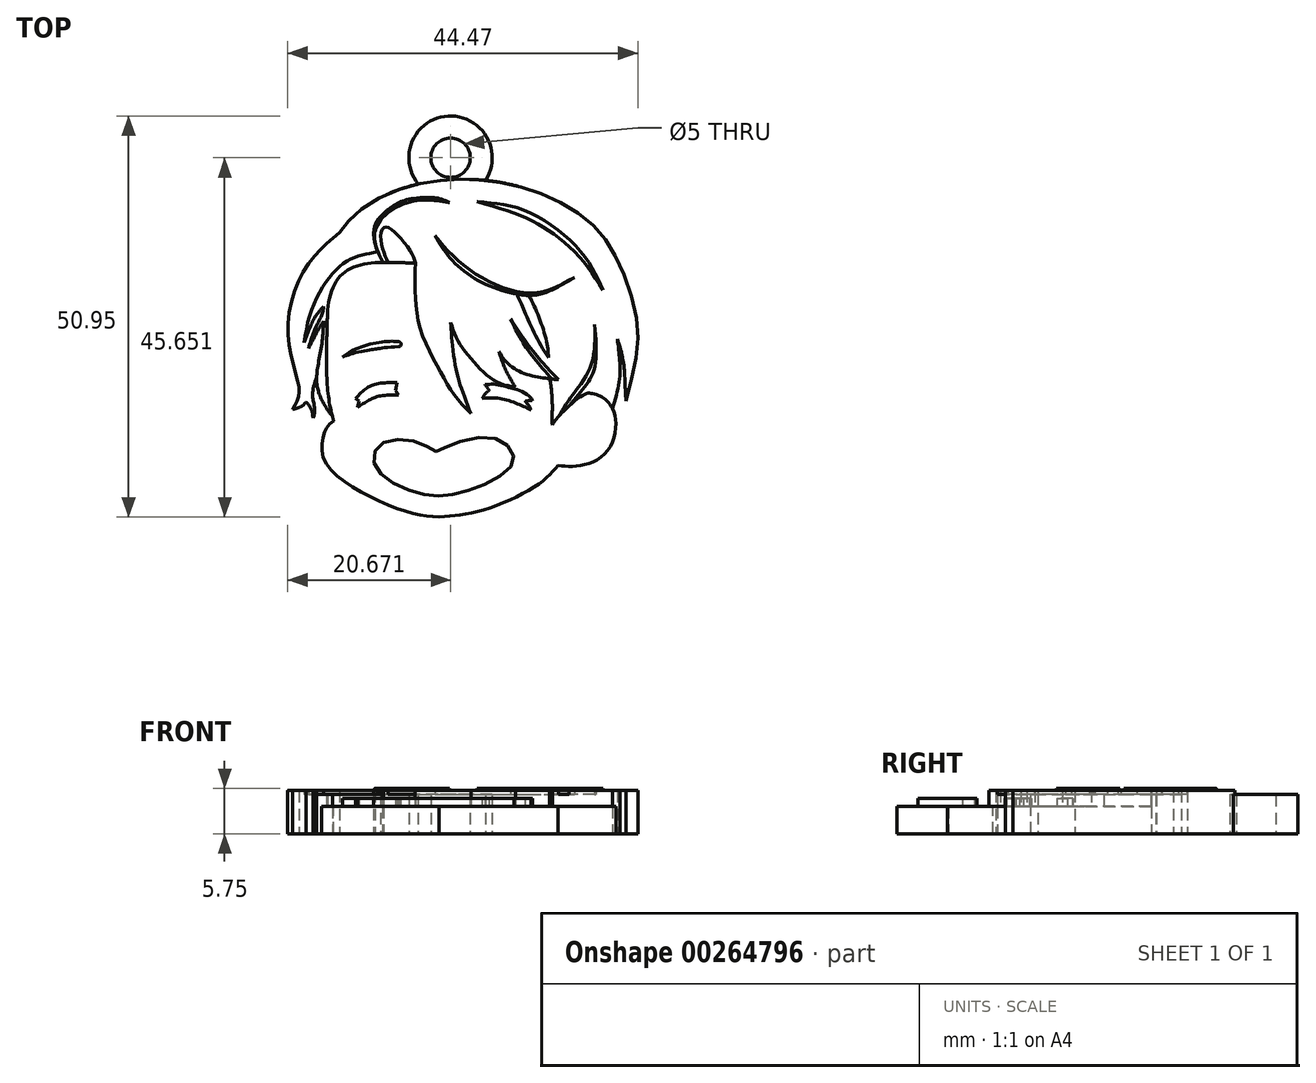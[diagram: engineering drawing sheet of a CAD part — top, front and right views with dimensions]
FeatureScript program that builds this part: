
annotation { "Feature Type Name" : "Feature", "Feature Type Description" : "" }
export const myFeature = defineFeature(function(context is Context, id is Id, definition is map)
    precondition{}
    {
        {
            var Q0;
            Q0=qCreatedBy(makeId("Top.planeOp"),FACE);
            var sketch = newSketch(context, id + "F0", { "sketchPlane" : qUnion([Q0])});
            skLineSegment(sketch, "E0", {"start": v(0, 26.14) * mm, "end": v(0, -13.86) * mm, "construction": true});
            skFitSpline(sketch, "E1", {"points": [v(-13.4, -3.41) * mm, v(-14.59, -4.9) * mm, v(-14.68, -8.16) * mm, v(-10.4, -12.17) * mm, v(-3.68, -15.06) * mm, v(0, -15.62) * mm], "startDerivative": vector(-13.93, -9.32) * mm, "endDerivative": vector(18.39, -1.5) * mm});
            skFitSpline(sketch, "E2", {"points": [v(0, -15.62) * mm, v(5.36, -14.78) * mm, v(12.63, -11.43) * mm, v(15.05, -9.1) * mm], "startDerivative": vector(14.98, 1.14) * mm, "endDerivative": vector(7.26, 8.68) * mm});
            skFitSpline(sketch, "E3", {"points": [v(15.05, -9.1) * mm, v(17.76, -9.1) * mm, v(21.2, -7.42) * mm, v(22.42, -3.41) * mm, v(21.58, -1.17) * mm, v(18.5, 0) * mm, v(15.05, -3.41) * mm, v(15.05, -4.25) * mm], "startDerivative": vector(18.97, -1.5) * mm, "endDerivative": vector(3.2, -10.24) * mm, "construction": true});
            skFitSpline(sketch, "E4", {"points": [v(14.37, -3.91) * mm, v(15.86, -2.1) * mm, v(18.5, 0) * mm, v(19.35, 0.08) * mm, v(20.48, -0.29) * mm, v(21.58, -1.17) * mm, v(22.42, -3.41) * mm, v(21.2, -7.42) * mm, v(17.76, -9.1) * mm, v(15.05, -9.1) * mm], "startDerivative": vector(9.94, 16.2) * mm, "endDerivative": vector(-21.45, 1.73) * mm});
            skFitSpline(sketch, "E5", {"points": [v(-14.19, 10.66) * mm, v(-12.54, 15.05) * mm, v(-8.76, 16.63) * mm, v(-3.04, 16.63) * mm], "startDerivative": vector(1.75, 16.5) * mm, "endDerivative": vector(16.06, -0.48) * mm});
            skFitSpline(sketch, "E6", {"points": [v(-3.04, 16.63) * mm, v(-3.04, 12.63) * mm, v(-2.33, 8) * mm, v(0, 3.15) * mm, v(1.82, 0) * mm, v(4.02, -2.5) * mm], "startDerivative": vector(-0.37, -20.1) * mm, "endDerivative": vector(13.1, -13.51) * mm});
            skFitSpline(sketch, "E7", {"points": [v(4.02, -2.5) * mm, v(2.77, 0.87) * mm, v(1.98, 3.93) * mm, v(1.56, 7.52) * mm, v(1.43, 9.09) * mm], "startDerivative": vector(-5.05, 13.03) * mm, "endDerivative": vector(-1.35, 13.2) * mm});
            skFitSpline(sketch, "E8", {"points": [v(1.43, 9.09) * mm, v(2.5, 6.55) * mm, v(4.66, 3.77) * mm, v(7.17, 1.61) * mm, v(9.69, 0.87) * mm], "startDerivative": vector(3.7, -10.7) * mm, "endDerivative": vector(11.1, -2.02) * mm});
            skFitSpline(sketch, "E9", {"points": [v(7.82, 5.39) * mm, v(9.13, 3.52) * mm, v(11.7, 2.36) * mm, v(15.14, 1.84) * mm, v(17.15, 1.84) * mm], "startDerivative": vector(4.7, -8.74) * mm, "endDerivative": vector(8.44, 0.3) * mm, "construction": true});
            skFitSpline(sketch, "E10", {"points": [v(14.01, 1.94) * mm, v(14.2, 0.87) * mm, v(14.32, -0.49) * mm, v(14.36, -2.2) * mm, v(14.37, -3.91) * mm], "startDerivative": vector(1.08, -4.56) * mm, "endDerivative": vector(1.1, -5.47) * mm});
            skFitSpline(sketch, "E11", {"points": [v(-13.4, -3.41) * mm, v(-14.31, 2.85) * mm, v(-14.19, 10.66) * mm], "startDerivative": vector(-3.96, 12.36) * mm, "endDerivative": vector(0.4, 15.4) * mm});
            skFitSpline(sketch, "E12", {"points": [v(-12.65, 20.52) * mm, v(-16.75, 16.37) * mm, v(-19.24, 8.2) * mm, v(-17.95, 1.51) * mm, v(-17.9, -0.43) * mm, v(-18.62, -1.94) * mm], "startDerivative": vector(-19.1, -15.5) * mm, "endDerivative": vector(-7.31, -11.74) * mm});
            skFitSpline(sketch, "E13", {"points": [v(-18.62, -1.94) * mm, v(-17.47, -1.53) * mm, v(-16.9, -0.98) * mm], "startDerivative": vector(2.3, 0.41) * mm, "endDerivative": vector(1.1, 1.36) * mm});
            skFitSpline(sketch, "E14", {"points": [v(-16.9, -0.98) * mm, v(-16.25, -1.94) * mm, v(-16.04, -3.02) * mm], "startDerivative": vector(1.51, -1.67) * mm, "endDerivative": vector(0.4, -2.4) * mm});
            skFitSpline(sketch, "E15", {"points": [v(-16.04, -3.02) * mm, v(-15.81, -1.94) * mm, v(-16.04, -0.8) * mm], "startDerivative": vector(0.92, 2.4) * mm, "endDerivative": vector(-0.88, 2.92) * mm, "construction": true});
            skFitSpline(sketch, "E16", {"points": [v(-16.04, -0.8) * mm, v(-16.04, 0.6) * mm, v(-15.58, 1.39) * mm], "startDerivative": vector(-0.2, 1.92) * mm, "endDerivative": vector(0.95, 1.57) * mm, "construction": true});
            skFitSpline(sketch, "E17", {"points": [v(-12.65, 20.52) * mm, v(-10.64, 22.9) * mm, v(-5.79, 25.74) * mm, v(0, 27.11) * mm, v(5.19, 27.21) * mm, v(10.8, 26.19) * mm, v(16.16, 23.92) * mm, v(20.2, 20.77) * mm, v(22.7, 16.89) * mm, v(24.9, 10.6) * mm, v(25.08, 5.27) * mm, v(23.71, -0.85) * mm], "startDerivative": vector(24.35, 34.26) * mm, "endDerivative": vector(-17.15, -63.7) * mm});
            skFitSpline(sketch, "E18", {"points": [v(22.61, 7) * mm, v(23.36, 4.37) * mm, v(23.57, 1.98) * mm, v(23.71, -0.85) * mm], "startDerivative": vector(2.65, -7.12) * mm, "endDerivative": vector(0.34, -7.37) * mm});
            skFitSpline(sketch, "E19", {"points": [v(22.61, 7) * mm, v(22.88, 4.69) * mm, v(22.88, 1.75) * mm, v(22.29, -1.24) * mm, v(22.05, -1.84) * mm], "startDerivative": vector(1.12, -8.58) * mm, "endDerivative": vector(-1.44, -3.33) * mm, "construction": true});
            skFitSpline(sketch, "E20", {"points": [v(22, -1.84) * mm, v(22.88, 1.75) * mm, v(22.88, 4.69) * mm, v(22.61, 7) * mm], "startDerivative": vector(2.87, 9.77) * mm, "endDerivative": vector(-1, 7.59) * mm});
            skFitSpline(sketch, "E21", {"points": [v(-15.58, 1.39) * mm, v(-15.19, -0.15) * mm, v(-14.34, -1.78) * mm, v(-13.58, -2.82) * mm], "startDerivative": vector(0.86, -4.54) * mm, "endDerivative": vector(2.6, -3.14) * mm});
            skFitSpline(sketch, "E22", {"points": [v(-10.64, -0.53) * mm, v(-9.31, 0.69) * mm, v(-7.93, 1.32) * mm, v(-5.39, 1.45) * mm], "startDerivative": vector(4.08, 4.14) * mm, "endDerivative": vector(7.18, -0.06) * mm});
            skFitSpline(sketch, "E23", {"points": [v(-10.64, -0.53) * mm, v(-10.2, -0.88) * mm], "startDerivative": vector(0.44, -0.35) * mm, "endDerivative": vector(0.44, -0.35) * mm});
            skFitSpline(sketch, "E24", {"points": [v(-10.2, -0.88) * mm, v(-10.4, -1.72) * mm], "startDerivative": vector(-0.2, -0.84) * mm, "endDerivative": vector(-0.2, -0.84) * mm});
            skFitSpline(sketch, "E25", {"points": [v(-10.4, -1.72) * mm, v(-9.13, -0.88) * mm, v(-7.65, -0.27) * mm, v(-5.2, -0.09) * mm], "startDerivative": vector(4.13, 2.9) * mm, "endDerivative": vector(6.8, 0.1) * mm});
            skFitSpline(sketch, "E26", {"points": [v(-5.39, 1.45) * mm, v(-5.55, 0.46) * mm], "startDerivative": vector(-0.16, -0.99) * mm, "endDerivative": vector(-0.16, -0.99) * mm});
            skFitSpline(sketch, "E27", {"points": [v(-5.55, 0.46) * mm, v(-5.2, -0.09) * mm], "startDerivative": vector(0.36, -0.54) * mm, "endDerivative": vector(0.36, -0.54) * mm});
            skFitSpline(sketch, "E28", {"points": [v(5.8, 1.2) * mm, v(7.17, 1.23) * mm, v(8.9, 0.84) * mm, v(10.2, 0.46) * mm, v(11.7, -0.53) * mm, v(11.82, -0.85) * mm], "startDerivative": vector(6.24, 0.69) * mm, "endDerivative": vector(0.25, -2.75) * mm});
            skFitSpline(sketch, "E29", {"points": [v(11.82, -0.85) * mm, v(11.29, -0.85) * mm, v(10.9, -0.92) * mm], "startDerivative": vector(-1.03, 0.04) * mm, "endDerivative": vector(-0.8, -0.2) * mm});
            skFitSpline(sketch, "E30", {"points": [v(10.9, -0.92) * mm, v(11.16, -1.19) * mm, v(11.5, -1.66) * mm, v(11.63, -2) * mm], "startDerivative": vector(0.8, -0.75) * mm, "endDerivative": vector(0.3, -1.03) * mm});
            skFitSpline(sketch, "E31", {"points": [v(11.63, -2) * mm, v(9.93, -1.23) * mm, v(7.6, -0.53) * mm, v(5.46, -0.53) * mm], "startDerivative": vector(-5.2, 2.45) * mm, "endDerivative": vector(-6.32, -0.48) * mm});
            skFitSpline(sketch, "E32", {"points": [v(5.8, 1.2) * mm, v(6.08, 0.86) * mm, v(6.35, 0.46) * mm], "startDerivative": vector(0.58, -0.66) * mm, "endDerivative": vector(0.51, -0.8) * mm});
            skFitSpline(sketch, "E33", {"points": [v(6.35, 0.46) * mm, v(5.9, 0.11) * mm, v(5.46, -0.53) * mm], "startDerivative": vector(-1.02, -0.57) * mm, "endDerivative": vector(-0.76, -1.38) * mm});
            skFitSpline(sketch, "E34", {"points": [v(-5.16, 6.68) * mm, v(-7.38, 6.62) * mm, v(-10.76, 5.64) * mm, v(-12.27, 4.73) * mm], "startDerivative": vector(-6.43, 0.3) * mm, "endDerivative": vector(-4.54, -3.28) * mm});
            skFitSpline(sketch, "E35", {"points": [v(-12.27, 4.73) * mm, v(-10.8, 5.2) * mm, v(-8.63, 5.65) * mm, v(-7.81, 5.78) * mm, v(-5.17, 6.02) * mm], "startDerivative": vector(5, 2.04) * mm, "endDerivative": vector(12.14, 0.39) * mm});
            skFitSpline(sketch, "E36", {"points": [v(-5.16, 6.68) * mm, v(-4.88, 6.48) * mm, v(-4.89, 6.15) * mm, v(-5.17, 6.02) * mm], "startDerivative": vector(1, -0.45) * mm, "endDerivative": vector(-1.03, -0.24) * mm});
            skFitSpline(sketch, "E37", {"points": [v(11.13, 4.5) * mm, v(8.62, 5.65) * mm, v(5.33, 6.3) * mm, v(3.94, 6.2) * mm, v(3.94, 5.88) * mm, v(6.12, 5.78) * mm, v(8.1, 5.39) * mm, v(11.13, 4.5) * mm]});
            skFitSpline(sketch, "E38", {"points": [v(-0.4, -7.32) * mm, v(-1.95, -6.4) * mm, v(-5.02, -5.77) * mm, v(-7.66, -6.54) * mm, v(-8.33, -8.3) * mm, v(-7.24, -10.32) * mm, v(-4.17, -12.08) * mm, v(-0.79, -12.9) * mm, v(1.96, -12.72) * mm, v(5.77, -11.45) * mm, v(8.91, -9.44) * mm, v(9.44, -7.78) * mm, v(8.1, -6.09) * mm, v(4.82, -5.52) * mm, v(0.45, -6.9) * mm, v(-0.4, -7.32) * mm]});
            skLineSegment(sketch, "E39.bottom", {"start": v(-9.61, -2.71) * mm, "end": v(-9.4, -2.71) * mm});
            skLineSegment(sketch, "E39.top", {"start": v(-9.61, -3.67) * mm, "end": v(-9.4, -3.67) * mm});
            skLineSegment(sketch, "E39.left", {"start": v(-9.61, -2.71) * mm, "end": v(-9.61, -3.67) * mm});
            skLineSegment(sketch, "E39.right", {"start": v(-9.4, -2.71) * mm, "end": v(-9.4, -3.67) * mm});
            skLineSegment(sketch, "E40.bottom", {"start": v(-8.16, -2.58) * mm, "end": v(-7.95, -2.58) * mm});
            skLineSegment(sketch, "E40.top", {"start": v(-8.16, -3.65) * mm, "end": v(-7.95, -3.65) * mm});
            skLineSegment(sketch, "E40.left", {"start": v(-8.16, -2.58) * mm, "end": v(-8.16, -3.65) * mm});
            skLineSegment(sketch, "E40.right", {"start": v(-7.95, -2.58) * mm, "end": v(-7.95, -3.65) * mm});
            skLineSegment(sketch, "E41.bottom", {"start": v(-6.18, -2.56) * mm, "end": v(-5.92, -2.56) * mm});
            skLineSegment(sketch, "E41.top", {"start": v(-6.18, -3.57) * mm, "end": v(-5.92, -3.57) * mm});
            skLineSegment(sketch, "E41.left", {"start": v(-6.18, -2.56) * mm, "end": v(-6.18, -3.57) * mm});
            skLineSegment(sketch, "E41.right", {"start": v(-5.92, -2.56) * mm, "end": v(-5.92, -3.57) * mm});
            skLineSegment(sketch, "E42.bottom", {"start": v(7.82, -3.54) * mm, "end": v(8.22, -3.54) * mm});
            skLineSegment(sketch, "E42.top", {"start": v(7.82, -4.76) * mm, "end": v(8.22, -4.76) * mm});
            skLineSegment(sketch, "E42.left", {"start": v(7.82, -3.54) * mm, "end": v(7.82, -4.76) * mm});
            skLineSegment(sketch, "E42.right", {"start": v(8.22, -3.54) * mm, "end": v(8.22, -4.76) * mm});
            skLineSegment(sketch, "E43.bottom", {"start": v(9.06, -3.54) * mm, "end": v(9.53, -3.54) * mm});
            skLineSegment(sketch, "E43.top", {"start": v(9.06, -4.83) * mm, "end": v(9.53, -4.83) * mm});
            skLineSegment(sketch, "E43.left", {"start": v(9.06, -3.54) * mm, "end": v(9.06, -4.83) * mm});
            skLineSegment(sketch, "E43.right", {"start": v(9.53, -3.54) * mm, "end": v(9.53, -4.83) * mm});
            skLineSegment(sketch, "E44.bottom", {"start": v(10.28, -3.46) * mm, "end": v(10.68, -3.46) * mm});
            skLineSegment(sketch, "E44.top", {"start": v(10.28, -4.8) * mm, "end": v(10.68, -4.8) * mm});
            skLineSegment(sketch, "E44.left", {"start": v(10.28, -3.46) * mm, "end": v(10.28, -4.8) * mm});
            skLineSegment(sketch, "E44.right", {"start": v(10.68, -3.46) * mm, "end": v(10.68, -4.8) * mm});
            skFitSpline(sketch, "E45", {"points": [v(-7.1, 16.74) * mm, v(-8, 18.64) * mm, v(-8.06, 21.96) * mm, v(-5.99, 24.33) * mm, v(-0.95, 24.57) * mm, v(1.6, 21.24) * mm, v(5.16, 17.15) * mm, v(11.1, 14.6) * mm, v(17.2, 14.84) * mm], "startDerivative": vector(-11.68, 19.6) * mm, "endDerivative": vector(41.04, 5.62) * mm});
            skFitSpline(sketch, "E46", {"points": [v(-2.9, 17.32) * mm, v(-3.04, 16.63) * mm], "startDerivative": vector(-0.15, -0.7) * mm, "endDerivative": vector(-0.15, -0.7) * mm});
            skFitSpline(sketch, "E47", {"points": [v(0.94, 15.14) * mm, v(1.16, 10.73) * mm, v(1.43, 9.09) * mm], "startDerivative": vector(0.23, -8) * mm, "endDerivative": vector(0.78, -3.78) * mm});
            skFitSpline(sketch, "E48", {"points": [v(9.69, 0.87) * mm, v(8.23, 3.55) * mm, v(6.79, 8.4) * mm, v(6.2, 11.37) * mm, v(5.56, 13.76) * mm], "startDerivative": vector(-6.27, 9.9) * mm, "endDerivative": vector(-3.25, 11.04) * mm});
            skFitSpline(sketch, "E49", {"points": [v(7.57, 5.4) * mm, v(9.13, 3.52) * mm, v(11.7, 2.36) * mm, v(14.01, 1.94) * mm, v(15.14, 1.84) * mm, v(17.15, 1.84) * mm], "startDerivative": vector(6.28, -9.53) * mm, "endDerivative": vector(11.25, 0.15) * mm});
            skFitSpline(sketch, "E50", {"points": [v(-8.36, 17.98) * mm, v(-12.22, 16.56) * mm, v(-16.6, 9.44) * mm, v(-17.2, 0.6) * mm, v(-16.9, -0.98) * mm], "startDerivative": vector(-17.57, -3.44) * mm, "endDerivative": vector(2.33, -8.82) * mm});
            skFitSpline(sketch, "E51", {"points": [v(-7.82, 18.1) * mm, v(-8.36, 17.98) * mm], "startDerivative": vector(-0.55, -0.12) * mm, "endDerivative": vector(-0.55, -0.12) * mm});
            skFitSpline(sketch, "E52", {"points": [v(-12.65, 20.52) * mm, v(-11.54, 21.12) * mm, v(-10.45, 21.41) * mm, v(-9.17, 21.45) * mm, v(-8.2, 21.3) * mm], "startDerivative": vector(5.65, 3.37) * mm, "endDerivative": vector(3.5, -0.93) * mm});
            skFitSpline(sketch, "E53", {"points": [v(18.77, 12.31) * mm, v(20.73, 10.42) * mm, v(22.61, 7) * mm], "startDerivative": vector(4.5, -3.68) * mm, "endDerivative": vector(3.22, -6.86) * mm});
            skFitSpline(sketch, "E54", {"points": [v(4.81, 24.45) * mm, v(11.09, 23.23) * mm, v(17.96, 18.13) * mm, v(20.81, 13.21) * mm], "startDerivative": vector(19.97, -1.65) * mm, "endDerivative": vector(7.33, -16.32) * mm});
            skFitSpline(sketch, "E55", {"points": [v(4.81, 24.45) * mm, v(10.55, 22.58) * mm, v(14.29, 20.5) * mm, v(17.96, 17.25) * mm, v(20.81, 13.21) * mm], "startDerivative": vector(23.36, -6.63) * mm, "endDerivative": vector(10.67, -16.96) * mm});
            skFitSpline(sketch, "E56", {"points": [v(-6.5, 16.74) * mm, v(-7.18, 18.45) * mm, v(-7.36, 20.62) * mm, v(-6.8, 21.21) * mm, v(-5.61, 20.53) * mm, v(-3.63, 18.1) * mm, v(-3.04, 16.63) * mm], "startDerivative": vector(-4.34, 9.22) * mm, "endDerivative": vector(2.53, -8.61) * mm});
            skFitSpline(sketch, "E57", {"points": [v(-2.59, 20.74) * mm, v(-2.9, 17.32) * mm], "startDerivative": vector(-0.3, -3.41) * mm, "endDerivative": vector(-0.3, -3.41) * mm});
            skFitSpline(sketch, "E58", {"points": [v(-0.51, 20.11) * mm, v(2.78, 16.63) * mm, v(7.79, 13.65) * mm, v(12.74, 12.94) * mm, v(17.2, 14.84) * mm], "startDerivative": vector(12.39, -14.82) * mm, "endDerivative": vector(17.86, 10.14) * mm});
            skFitSpline(sketch, "E59", {"points": [v(-0.51, 20.11) * mm, v(0.91, 17.86) * mm, v(4.65, 14.6) * mm, v(9.86, 12.7) * mm, v(13.16, 12.79) * mm, v(17.2, 14.84) * mm], "startDerivative": vector(7.39, -13.6) * mm, "endDerivative": vector(20.75, 11.78) * mm});
            skFitSpline(sketch, "E60", {"points": [v(0.94, 15.14) * mm, v(0.76, 17.22) * mm, v(0.38, 18.59) * mm], "startDerivative": vector(-0.2, 4.02) * mm, "endDerivative": vector(-0.94, 2.85) * mm});
            skFitSpline(sketch, "E61", {"points": [v(9.86, 12.7) * mm, v(10.79, 10.58) * mm, v(12.98, 6.07) * mm, v(15.58, 2.68) * mm, v(17.15, 1.84) * mm], "startDerivative": vector(3.94, -8.95) * mm, "endDerivative": vector(8.2, -3.2) * mm});
            skFitSpline(sketch, "E62", {"points": [v(13.87, 4.65) * mm, v(13.67, 6.45) * mm, v(12.7, 9.67) * mm, v(11.43, 12.54) * mm], "startDerivative": vector(-0.38, 6.12) * mm, "endDerivative": vector(-3.67, 7.7) * mm});
            skFitSpline(sketch, "E63", {"points": [v(9.07, 9.53) * mm, v(10.98, 6) * mm, v(14.32, 1.9) * mm], "startDerivative": vector(3.61, -7.54) * mm, "endDerivative": vector(6.8, -7.7) * mm});
            skFitSpline(sketch, "E64", {"points": [v(9.07, 9.53) * mm, v(12.15, 5.15) * mm, v(15.14, 1.84) * mm], "startDerivative": vector(5.78, -8.75) * mm, "endDerivative": vector(6.37, -6.58) * mm});
            skFitSpline(sketch, "E65", {"points": [v(19.74, 8.86) * mm, v(19.24, 3.54) * mm, v(16.86, -0.2) * mm, v(15.14, -2.86) * mm], "startDerivative": vector(0.33, -15.04) * mm, "endDerivative": vector(-5.4, -9.03) * mm});
            skFitSpline(sketch, "E66", {"points": [v(19.74, 8.86) * mm, v(19.74, 3.35) * mm, v(18.47, 0.94) * mm, v(16.49, -1.5) * mm], "startDerivative": vector(1.23, -15.1) * mm, "endDerivative": vector(-6.75, -8.1) * mm});
            skFitSpline(sketch, "E67", {"points": [v(-15.58, 1.39) * mm, v(-15.24, 3.23) * mm, v(-14.32, 5.78) * mm], "startDerivative": vector(0.5, 3.93) * mm, "endDerivative": vector(2, 4.83) * mm, "construction": true});
            skFitSpline(sketch, "E68", {"points": [v(-14.32, 6.05) * mm, v(-15.81, 1.46) * mm, v(-16.1, -0.15) * mm, v(-15.95, -1.08) * mm, v(-15.86, -2.42) * mm, v(-16.04, -3.02) * mm], "startDerivative": vector(-5.21, -14.88) * mm, "endDerivative": vector(-1.79, -4.23) * mm});
            skFitSpline(sketch, "E69", {"points": [v(-14.69, 11.1) * mm, v(-15.81, 9.72) * mm, v(-17.15, 6.53) * mm], "startDerivative": vector(-2.78, -2.86) * mm, "endDerivative": vector(-2.16, -6.12) * mm});
            skFitSpline(sketch, "E70", {"points": [v(-14.69, 11.1) * mm, v(-14.96, 9.97) * mm, v(-15.81, 8.24) * mm, v(-16.6, 5.78) * mm], "startDerivative": vector(-0.66, -4.16) * mm, "endDerivative": vector(-1.75, -6.5) * mm});
            skFitSpline(sketch, "E71", {"points": [v(-16.6, 5.78) * mm, v(-15.5, 7.96) * mm, v(-14.69, 9.26) * mm], "startDerivative": vector(2.02, 4.17) * mm, "endDerivative": vector(1.8, 2.73) * mm});
            skFitSpline(sketch, "E72", {"points": [v(-14.69, 9.26) * mm, v(-14.96, 6.05) * mm, v(-15.5, 3.02) * mm, v(-15.58, 1.39) * mm], "startDerivative": vector(-0.44, -8.55) * mm, "endDerivative": vector(0.02, -5.67) * mm});
            skFitSpline(sketch, "E73", {"points": [v(-7.1, 16.74) * mm, v(-7.82, 18.1) * mm, v(-8.2, 21.3) * mm, v(-5.99, 23.82) * mm, v(-4.13, 24.68) * mm, v(-0.57, 24.95) * mm, v(1.3, 24.33) * mm], "startDerivative": vector(-5.55, 8.97) * mm, "endDerivative": vector(12, -5.66) * mm});
            skFitSpline(sketch, "E74", {"points": [v(1.3, 24.33) * mm, v(-0.44, 24.6) * mm, v(-4.02, 24.33) * mm, v(-7.42, 22.13) * mm, v(-8.22, 19.85) * mm, v(-7.1, 16.57) * mm], "startDerivative": vector(-10.24, 2) * mm, "endDerivative": vector(7.31, -15.93) * mm});
            skSolve(sketch);
        }
        {
            var Q0;
            {var subQ4=sQuery(id+"F0.wireOp",EDGE,"E1");Q0=makeQuery(id+"F0.imprint","IMPRINT",FACE,{"disambiguationData":[TD([[makeQuery(id+"F0.imprint","IMPRINT",EDGE,{"derivedFrom":subQ4}),1.0]])]});}
            var Q1;
            Q1=makeQuery(id+"F0.imprint","IMPRINT",FACE,{"disambiguationData":[TD([[makeQuery(id+"F0.imprint","IMPRINT",EDGE,{"derivedFrom":sQuery(id+"F0.wireOp",EDGE,"E39.bottom")}),-1.0]])]});
            var Q2;
            Q2=makeQuery(id+"F0.imprint","IMPRINT",FACE,{"disambiguationData":[TD([[makeQuery(id+"F0.imprint","IMPRINT",EDGE,{"derivedFrom":sQuery(id+"F0.wireOp",EDGE,"E40.bottom")}),-1.0]])]});
            var Q3;
            Q3=makeQuery(id+"F0.imprint","IMPRINT",FACE,{"disambiguationData":[TD([[makeQuery(id+"F0.imprint","IMPRINT",EDGE,{"derivedFrom":sQuery(id+"F0.wireOp",EDGE,"E41.bottom")}),-1.0]])]});
            var Q4;
            Q4=makeQuery(id+"F0.imprint","IMPRINT",FACE,{"disambiguationData":[TD([[makeQuery(id+"F0.imprint","IMPRINT",EDGE,{"derivedFrom":sQuery(id+"F0.wireOp",EDGE,"E42.bottom")}),-1.0]])]});
            var Q5;
            Q5=makeQuery(id+"F0.imprint","IMPRINT",FACE,{"disambiguationData":[TD([[makeQuery(id+"F0.imprint","IMPRINT",EDGE,{"derivedFrom":sQuery(id+"F0.wireOp",EDGE,"E43.bottom")}),-1.0]])]});
            var Q6;
            Q6=makeQuery(id+"F0.imprint","IMPRINT",FACE,{"disambiguationData":[TD([[makeQuery(id+"F0.imprint","IMPRINT",EDGE,{"derivedFrom":sQuery(id+"F0.wireOp",EDGE,"E44.bottom")}),-1.0]])]});
            extrude(context, id + "F1", {"entities" : qUnion([Q0, Q1, Q2, Q3, Q4, Q5, Q6]), "depth" : 3.5 * mm, "offsetDistance" : 25 * mm});
        }
        {
            var Q0;
            Q0=makeQuery(id+"F0.imprint","IMPRINT",FACE,{"disambiguationData":[TD([[makeQuery(id+"F0.imprint","IMPRINT",EDGE,{"derivedFrom":sQuery(id+"F0.wireOp",EDGE,"E34")}),1.0]])]});
            var Q1;
            Q1=makeQuery(id+"F0.imprint","IMPRINT",FACE,{"disambiguationData":[TD([[makeQuery(id+"F0.imprint","IMPRINT",EDGE,{"derivedFrom":sQuery(id+"F0.wireOp",EDGE,"E38")}),1.0]])]});
            var Q2;
            Q2=makeQuery(id+"F0.imprint","IMPRINT",FACE,{"disambiguationData":[TD([[makeQuery(id+"F0.imprint","IMPRINT",EDGE,{"derivedFrom":sQuery(id+"F0.wireOp",EDGE,"E22")}),-1.0]])]});
            var Q3;
            Q3=makeQuery(id+"F0.imprint","IMPRINT",FACE,{"disambiguationData":[TD([[makeQuery(id+"F0.imprint","IMPRINT",EDGE,{"derivedFrom":sQuery(id+"F0.wireOp",EDGE,"E28")}),-1.0]])]});
            extrude(context, id + "F2", {"entities" : qUnion([Q0, Q1, Q2, Q3]), "operationType" : NewBodyOperationType.ADD, "depth" : 4.5 * mm, "offsetDistance" : 25 * mm});
        }
        {
            var Q0;
            Q0=qCreatedBy(makeId("Top.planeOp"),FACE);
            var sketch = newSketch(context, id + "F3", { "sketchPlane" : qUnion([Q0])});
            skCircle(sketch, "E75", {"center": v(1.43, 30.03) * mm, "radius": 5.3 * mm});
            skCircle(sketch, "E76", {"center": v(1.43, 30.03) * mm, "radius": 2.5 * mm});
            skLineSegment(sketch, "E77", {"start": v(-1.07, 30.03) * mm, "end": v(3.93, 30.03) * mm, "construction": true});
            skSolve(sketch);
        }
        {
            var Q0;
            Q0=makeQuery(id+"F3.imprint","IMPRINT",FACE,{"disambiguationData":[TD([[makeQuery(id+"F3.imprint","IMPRINT",EDGE,{"derivedFrom":sQuery(id+"F3.wireOp",EDGE,"E75")}),1.0]])]});
            extrude(context, id + "F4", {"entities" : qUnion([Q0]), "operationType" : NewBodyOperationType.ADD, "depth" : 5 * mm, "offsetDistance" : 25 * mm});
        }
        {
            var Q0;
            {var subQ0=sQuery(id+"F0.wireOp",EDGE,"3d75d4a1-2e93-4ac8-ad39-6bc05c0790d6");var subQ12=makeQuery(id+"F0.imprint","IMPRINT",VERTEX,{"derivedFrom":subQ0});Q0=makeQuery(id+"F0.imprint","IMPRINT",FACE,{"disambiguationData":[TD([[makeQuery(id+"F0.imprint","IMPRINT",EDGE,{"disambiguationData":[TD([[subQ12,1.0]])],"derivedFrom":subQ0}),1.0]])]});}
            var Q1;
            Q1=makeQuery(id+"F0.imprint","IMPRINT",FACE,{"disambiguationData":[TD([[makeQuery(id+"F0.imprint","IMPRINT",EDGE,{"derivedFrom":sQuery(id+"F0.wireOp",EDGE,"E12")}),1.0]])]});
            var Q2;
            {var subQ0=sQuery(id+"F0.wireOp",EDGE,"E46");Q2=makeQuery(id+"F0.imprint","IMPRINT",FACE,{"disambiguationData":[TD([[makeQuery(id+"F0.imprint","IMPRINT",EDGE,{"derivedFrom":subQ0}),-1.0]])]});}
            var Q3;
            Q3=makeQuery(id+"F0.imprint","IMPRINT",FACE,{"disambiguationData":[TD([[makeQuery(id+"F0.imprint","IMPRINT",EDGE,{"derivedFrom":sQuery(id+"F0.wireOp",EDGE,"E14")}),1.0]])]});
            var Q4;
            Q4=makeQuery(id+"F0.imprint","IMPRINT",FACE,{"disambiguationData":[TD([[makeQuery(id+"F0.imprint","IMPRINT",EDGE,{"derivedFrom":sQuery(id+"F0.wireOp",EDGE,"E6")}),1.0]])]});
            var Q5;
            {var subQ8=sQuery(id+"F0.wireOp",EDGE,"E8");Q5=makeQuery(id+"F0.imprint","IMPRINT",FACE,{"disambiguationData":[TD([[makeQuery(id+"F0.imprint","IMPRINT",EDGE,{"derivedFrom":subQ8}),1.0]])]});}
            var Q6;
            {var subQ7=sQuery(id+"F0.wireOp",EDGE,"0a68ed68-5c6f-465a-9fe5-a1ceb8f8f996");Q6=makeQuery(id+"F0.imprint","IMPRINT",FACE,{"disambiguationData":[TD([[makeQuery(id+"F0.imprint","IMPRINT",EDGE,{"derivedFrom":subQ7}),-1.0]])]});}
            var Q7;
            {var subQ0=sQuery(id+"F0.wireOp",EDGE,"E48");var subQ1=sQuery(id+"F0.wireOp",EDGE,"E37");var subQ2=makeQuery(id+"F0.imprint","INTERSECT",VERTEX,{"disambiguationData":[OD(0.0)],"derivedFrom":[subQ1,subQ0]});Q7=makeQuery(id+"F0.imprint","IMPRINT",FACE,{"disambiguationData":[TD([[makeQuery(id+"F0.imprint","IMPRINT",EDGE,{"disambiguationData":[TD([[subQ2,1.0]])],"derivedFrom":subQ1}),1.0]])]});}
            var Q8;
            {var subQ4=sQuery(id+"F0.wireOp",EDGE,"E10");Q8=makeQuery(id+"F0.imprint","IMPRINT",FACE,{"disambiguationData":[TD([[makeQuery(id+"F0.imprint","IMPRINT",EDGE,{"derivedFrom":subQ4}),1.0]])]});}
            var Q9;
            {var subQ0=sQuery(id+"F0.wireOp",EDGE,"E20");Q9=makeQuery(id+"F0.imprint","IMPRINT",FACE,{"disambiguationData":[TD([[makeQuery(id+"F0.imprint","IMPRINT",EDGE,{"derivedFrom":subQ0}),1.0]])]});}
            var Q10;
            Q10=makeQuery(id+"F0.imprint","IMPRINT",FACE,{"disambiguationData":[TD([[makeQuery(id+"F0.imprint","IMPRINT",EDGE,{"derivedFrom":sQuery(id+"F0.wireOp",EDGE,"E17")}),-1.0]])]});
            var Q11;
            Q11=makeQuery(id+"F0.imprint","IMPRINT",FACE,{"disambiguationData":[TD([[makeQuery(id+"F0.imprint","IMPRINT",EDGE,{"derivedFrom":sQuery(id+"F0.wireOp",EDGE,"E54")}),-1.0]])]});
            var Q12;
            {var subQ0=sQuery(id+"F0.wireOp",EDGE,"E48");var subQ1=sQuery(id+"F0.wireOp",EDGE,"E37");var subQ2=makeQuery(id+"F0.imprint","INTERSECT",VERTEX,{"disambiguationData":[OD(0.0)],"derivedFrom":[subQ1,subQ0]});Q12=makeQuery(id+"F0.imprint","IMPRINT",FACE,{"disambiguationData":[TD([[makeQuery(id+"F0.imprint","IMPRINT",EDGE,{"disambiguationData":[TD([[subQ2,-1.0]])],"derivedFrom":subQ1}),1.0]])]});}
            var Q13;
            {var subQ0=sQuery(id+"F0.wireOp",EDGE,"E73");var subQ1=sQuery(id+"F0.wireOp",EDGE,"E45");var subQ3=makeQuery(id+"F0.imprint","INTERSECT",VERTEX,{"disambiguationData":[OD(1.0)],"derivedFrom":[subQ1,subQ0]});Q13=makeQuery(id+"F0.imprint","IMPRINT",FACE,{"disambiguationData":[TD([[makeQuery(id+"F0.imprint","IMPRINT",EDGE,{"disambiguationData":[TD([[subQ3,1.0]])],"derivedFrom":subQ1}),-1.0]])]});}
            extrude(context, id + "F5", {"entities" : qUnion([Q0, Q1, Q2, Q3, Q4, Q5, Q6, Q7, Q8, Q9, Q10, Q11, Q12, Q13]), "operationType" : NewBodyOperationType.ADD, "depth" : 5.5 * mm, "offsetDistance" : 25 * mm});
        }
        {
            var Q0;
            {var subQ0=sQuery(id+"F0.wireOp",EDGE,"E56");Q0=makeQuery(id+"F0.imprint","IMPRINT",FACE,{"disambiguationData":[TD([[makeQuery(id+"F0.imprint","IMPRINT",EDGE,{"derivedFrom":subQ0}),-1.0]])]});}
            var Q1;
            {var subQ0=sQuery(id+"F0.wireOp",EDGE,"E65");Q1=makeQuery(id+"F0.imprint","IMPRINT",FACE,{"disambiguationData":[TD([[makeQuery(id+"F0.imprint","IMPRINT",EDGE,{"derivedFrom":subQ0}),1.0]])]});}
            var Q2;
            {var subQ4=sQuery(id+"F0.wireOp",EDGE,"E58");Q2=makeQuery(id+"F0.imprint","IMPRINT",FACE,{"disambiguationData":[TD([[makeQuery(id+"F0.imprint","IMPRINT",EDGE,{"derivedFrom":subQ4}),-1.0]])]});}
            var Q3;
            {var subQ0=sQuery(id+"F0.wireOp",EDGE,"E63");Q3=makeQuery(id+"F0.imprint","IMPRINT",FACE,{"disambiguationData":[TD([[makeQuery(id+"F0.imprint","IMPRINT",EDGE,{"derivedFrom":subQ0}),1.0]])]});}
            var Q4;
            {var subQ0=sQuery(id+"F0.wireOp",EDGE,"E51");Q4=makeQuery(id+"F0.imprint","IMPRINT",FACE,{"disambiguationData":[TD([[makeQuery(id+"F0.imprint","IMPRINT",EDGE,{"derivedFrom":subQ0}),1.0]])]});}
            var Q5;
            {var subQ0=sQuery(id+"F0.wireOp",EDGE,"E21");Q5=makeQuery(id+"F0.imprint","IMPRINT",FACE,{"disambiguationData":[TD([[makeQuery(id+"F0.imprint","IMPRINT",EDGE,{"derivedFrom":subQ0}),1.0]])]});}
            extrude(context, id + "F6", {"entities" : qUnion([Q0, Q1, Q2, Q3, Q4, Q5]), "operationType" : NewBodyOperationType.ADD, "depth" : 5 * mm, "offsetDistance" : 25 * mm});
        }
        {
            var Q0;
            {var subQ3=sQuery(id+"F0.wireOp",EDGE,"E62");Q0=makeQuery(id+"F0.imprint","IMPRINT",FACE,{"disambiguationData":[TD([[makeQuery(id+"F0.imprint","IMPRINT",EDGE,{"derivedFrom":subQ3}),1.0]])]});}
            var Q1;
            Q1=makeQuery(id+"F0.imprint","IMPRINT",FACE,{"disambiguationData":[TD([[makeQuery(id+"F0.imprint","IMPRINT",EDGE,{"derivedFrom":sQuery(id+"F0.wireOp",EDGE,"E54")}),-1.0]])]});
            var Q2;
            {var subQ0=sQuery(id+"F0.wireOp",EDGE,"E73");var subQ1=sQuery(id+"F0.wireOp",EDGE,"E45");var subQ5=makeQuery(id+"F0.imprint","INTERSECT",VERTEX,{"disambiguationData":[OD(1.0)],"derivedFrom":[subQ1,subQ0]});Q2=makeQuery(id+"F0.imprint","IMPRINT",FACE,{"disambiguationData":[TD([[makeQuery(id+"F0.imprint","IMPRINT",EDGE,{"disambiguationData":[TD([[subQ5,-1.0]])],"derivedFrom":subQ1}),-1.0]])]});}
            var Q3;
            {var subQ0=sQuery(id+"F0.wireOp",EDGE,"E73");var subQ1=sQuery(id+"F0.wireOp",EDGE,"E45");var subQ2=makeQuery(id+"F0.imprint","INTERSECT",VERTEX,{"disambiguationData":[OD(1.0)],"derivedFrom":[subQ1,subQ0]});Q3=makeQuery(id+"F0.imprint","IMPRINT",FACE,{"disambiguationData":[TD([[makeQuery(id+"F0.imprint","IMPRINT",EDGE,{"disambiguationData":[TD([[subQ2,-1.0]])],"derivedFrom":subQ1}),1.0]])]});}
            extrude(context, id + "F7", {"entities" : qUnion([Q0, Q1, Q2, Q3]), "operationType" : NewBodyOperationType.ADD, "depth" : 5.75 * mm, "offsetDistance" : 25 * mm});
        }
    });
